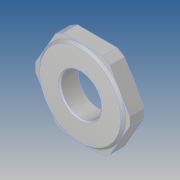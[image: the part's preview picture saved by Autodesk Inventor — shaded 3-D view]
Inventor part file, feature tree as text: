
AUTODESK INVENTOR PART (.ipt)
format: ipt  version: 2019 (Build 230136000, 136)  size: 143,360 bytes
history: native  units: mm
features: chamfer x3, sketch x3, extrude x2, other x2, hole x1
ambient origin geometry x8: Origin, YZ Plane, XZ Plane, XY Plane, X Axis, Y Axis, Z Axis, Center Point
bodies: Solide1 (feature_tree)
feature tree (11):
  extrude  "Extrusion1"  Depth=16.5mm
  chamfer  "Chanfrein1"  Distance=35.0mm
  chamfer  "Chanfrein2"  Distance=8.0mm
  other  "Plan de construction1"
  extrude  "Extrusion2"  Depth=0.5mm TaperAngle=45.0deg
  chamfer  "Chanfrein3"  Distance=1.0mm Angle=45.0deg
  hole  "Perçage1"  [1 undecoded]
  sketch  "Esquisse1"
  sketch  "Esquisse3"
  sketch  "Esquisse4"
  other  "Projeter les arêtes coupées1"
note: 1 required parameter value undecoded (feature->parameter linkage not recoverable at this tier; creation-order binding heuristic only, values carry confidence <= 0.55)
